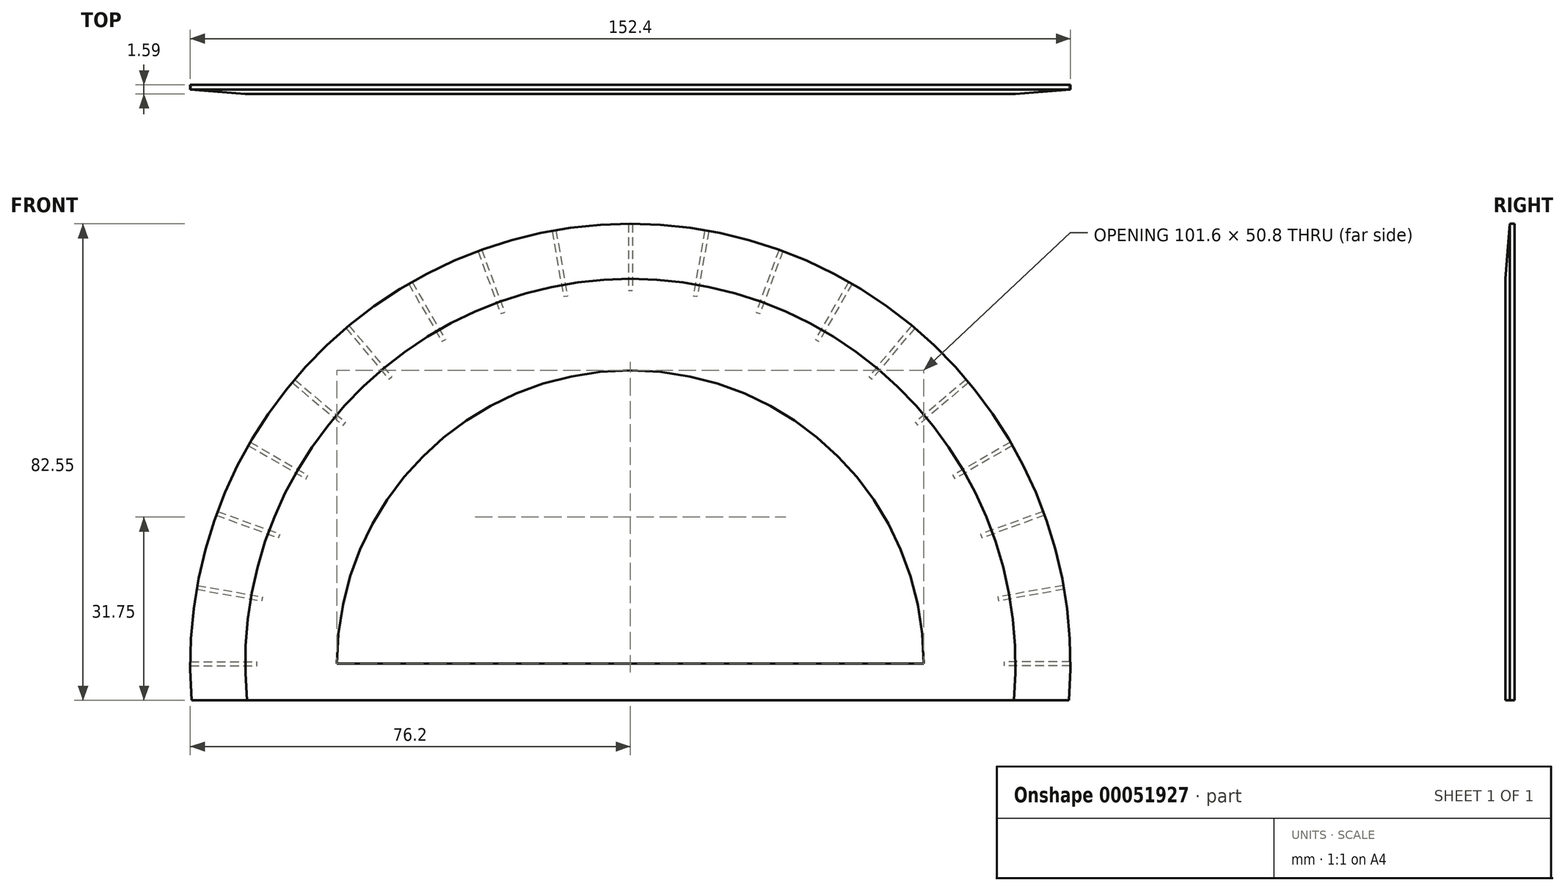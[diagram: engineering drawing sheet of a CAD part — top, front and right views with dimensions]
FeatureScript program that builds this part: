
annotation { "Feature Type Name" : "Feature", "Feature Type Description" : "" }
export const myFeature = defineFeature(function(context is Context, id is Id, definition is map)
    precondition{}
    {
        {
            var Q0;
            Q0=qCreatedBy(makeId("Front.planeOp"),FACE);
            var sketch = newSketch(context, id + "F0", { "sketchPlane" : qUnion([Q0])});
            skCircle(sketch, "E0", {"center": v(0, 0) * mm, "radius": 76.2 * mm});
            skCircle(sketch, "E1", {"center": v(0, 0) * mm, "radius": 50.8 * mm});
            skLineSegment(sketch, "E2", {"start": v(-50.8, 0) * mm, "end": v(50.8, 0) * mm});
            skLineSegment(sketch, "E3", {"start": v(-44, -25.4) * mm, "end": v(44, -25.4) * mm});
            skSolve(sketch);
        }
        {
            var Q0;
            Q0=makeQuery(id+"F0.imprint","IMPRINT",FACE,{"disambiguationData":[TD([[makeQuery(id+"F0.imprint","IMPRINT",EDGE,{"derivedFrom":sQuery(id+"F0.wireOp",EDGE,"E0")}),1.0]])]});
            var Q1;
            {var subQ0=sQuery(id+"F0.wireOp",EDGE,"E2");Q1=makeQuery(id+"F0.imprint","IMPRINT",FACE,{"disambiguationData":[TD([[makeQuery(id+"F0.imprint","IMPRINT",EDGE,{"derivedFrom":subQ0}),-1.0]])]});}
            extrude(context, id + "F1", {"entities" : qUnion([Q0, Q1]), "depth" : 1.59 * mm});
        }
        {
            var Q0;
            Q0=qCreatedBy(makeId("Top.planeOp"),FACE);
            var sketch = newSketch(context, id + "F2", { "sketchPlane" : qUnion([Q0])});
            skLineSegment(sketch, "E4", {"start": v(76.2, 0) * mm, "end": v(76.2, -1.59) * mm, "construction": true});
            skLineSegment(sketch, "E5.0", {"start": v(76.2, -1.59) * mm, "end": v(-76.2, -1.59) * mm, "construction": true});
            skLineSegment(sketch, "E6", {"start": v(76.2, -0.8) * mm, "end": v(66.67, -1.59) * mm});
            skLineSegment(sketch, "E7", {"start": v(66.67, -1.59) * mm, "end": v(76.2, -1.59) * mm});
            skLineSegment(sketch, "E8", {"start": v(0, 17.15) * mm, "end": v(0, -24.9) * mm, "construction": true});
            skLineSegment(sketch, "E9", {"start": v(76.2, -0.8) * mm, "end": v(76.2, -1.59) * mm});
            skSolve(sketch);
        }
        {
            var Q0;
            Q0=makeQuery(id+"F2.imprint","IMPRINT",FACE,{"disambiguationData":[TD([[makeQuery(id+"F2.imprint","IMPRINT",EDGE,{"derivedFrom":sQuery(id+"F2.wireOp",EDGE,"E6")}),1.0]])]});
            var Q1;
            Q1=sQuery(id+"F2.wireOp",EDGE,"E9");
            var Q2;
            Q2=sQuery(id+"F2.wireOp",EDGE,"E6");
            var Q3;
            Q3=sQuery(id+"F2.wireOp",EDGE,"E7");
            var Q4;
            Q4=sQuery(id+"F2.wireOp",EDGE,"E8");
            revolve(context, id + "F3", {"operationType" : NewBodyOperationType.REMOVE, "entities" : qUnion([Q0]), "surfaceEntities" : qUnion([Q1, Q2, Q3]), "axis" : qUnion([Q4]), "revolveType" : RevolveType.FULL, "oppositeDirection" : true});
        }
        {
            var Q0;
            Q0=makeQuery(id+"F1.opExtrude","CAP_FACE",FACE,{"disambiguationData":[OSD([sQuery(id+"F0.wireOp",EDGE,"E0"),sQuery(id+"F0.wireOp",EDGE,"E1"),sQuery(id+"F0.wireOp",EDGE,"E2"),sQuery(id+"F0.wireOp",EDGE,"E3")])],"isStart":true});
            var sketch = newSketch(context, id + "F4", { "sketchPlane" : qUnion([Q0])});
            skLineSegment(sketch, "E10.rect.bottom", {"start": v(76.2, -0.35) * mm, "end": v(64.66, -0.35) * mm});
            skLineSegment(sketch, "E10.rect.top", {"start": v(76.2, 0.35) * mm, "end": v(64.66, 0.35) * mm});
            skLineSegment(sketch, "E10.rect.left", {"start": v(76.2, -0.35) * mm, "end": v(76.2, 0.35) * mm});
            skLineSegment(sketch, "E10.rect.right", {"start": v(64.66, -0.35) * mm, "end": v(64.66, 0.35) * mm});
            skPoint(sketch, "E10.rect.middle", {"position": v(70.43, 0) * mm});
            skLineSegment(sketch, "E11.1.0", {"start": v(75.1, 12.9) * mm, "end": v(63.74, 10.89) * mm});
            skLineSegment(sketch, "E11.1.1", {"start": v(74.98, 13.57) * mm, "end": v(63.62, 11.57) * mm});
            skPoint(sketch, "E11.1.2", {"position": v(69.36, 12.23) * mm});
            skLineSegment(sketch, "E11.1.3", {"start": v(75.1, 12.9) * mm, "end": v(74.98, 13.57) * mm});
            skLineSegment(sketch, "E11.1.4", {"start": v(63.74, 10.89) * mm, "end": v(63.62, 11.57) * mm});
            skLineSegment(sketch, "E11.2.0", {"start": v(71.72, 25.74) * mm, "end": v(60.88, 21.8) * mm});
            skLineSegment(sketch, "E11.2.1", {"start": v(71.49, 26.39) * mm, "end": v(60.65, 22.44) * mm});
            skPoint(sketch, "E11.2.2", {"position": v(66.18, 24.09) * mm});
            skLineSegment(sketch, "E11.2.3", {"start": v(71.72, 25.74) * mm, "end": v(71.49, 26.39) * mm});
            skLineSegment(sketch, "E11.2.4", {"start": v(60.88, 21.8) * mm, "end": v(60.65, 22.44) * mm});
            skLineSegment(sketch, "E11.3.0", {"start": v(66.16, 37.8) * mm, "end": v(56.17, 32.03) * mm});
            skLineSegment(sketch, "E11.3.1", {"start": v(65.82, 38.4) * mm, "end": v(55.83, 32.63) * mm});
            skPoint(sketch, "E11.3.2", {"position": v(61, 35.22) * mm});
            skLineSegment(sketch, "E11.3.3", {"start": v(66.16, 37.8) * mm, "end": v(65.82, 38.4) * mm});
            skLineSegment(sketch, "E11.3.4", {"start": v(56.17, 32.03) * mm, "end": v(55.83, 32.63) * mm});
            skLineSegment(sketch, "E11.4.0", {"start": v(58.6, 48.71) * mm, "end": v(49.76, 41.3) * mm});
            skLineSegment(sketch, "E11.4.1", {"start": v(58.15, 49.25) * mm, "end": v(49.31, 41.83) * mm});
            skPoint(sketch, "E11.4.2", {"position": v(53.95, 45.27) * mm});
            skLineSegment(sketch, "E11.4.3", {"start": v(58.6, 48.71) * mm, "end": v(58.15, 49.25) * mm});
            skLineSegment(sketch, "E11.4.4", {"start": v(49.76, 41.3) * mm, "end": v(49.31, 41.83) * mm});
            skLineSegment(sketch, "E11.5.0", {"start": v(49.25, 58.15) * mm, "end": v(41.83, 49.31) * mm});
            skLineSegment(sketch, "E11.5.1", {"start": v(48.71, 58.6) * mm, "end": v(41.3, 49.76) * mm});
            skPoint(sketch, "E11.5.2", {"position": v(45.27, 53.95) * mm});
            skLineSegment(sketch, "E11.5.3", {"start": v(49.25, 58.15) * mm, "end": v(48.71, 58.6) * mm});
            skLineSegment(sketch, "E11.5.4", {"start": v(41.83, 49.31) * mm, "end": v(41.3, 49.76) * mm});
            skLineSegment(sketch, "E11.6.0", {"start": v(38.4, 65.82) * mm, "end": v(32.63, 55.83) * mm});
            skLineSegment(sketch, "E11.6.1", {"start": v(37.8, 66.16) * mm, "end": v(32.03, 56.17) * mm});
            skPoint(sketch, "E11.6.2", {"position": v(35.22, 61) * mm});
            skLineSegment(sketch, "E11.6.3", {"start": v(38.4, 65.82) * mm, "end": v(37.8, 66.16) * mm});
            skLineSegment(sketch, "E11.6.4", {"start": v(32.63, 55.83) * mm, "end": v(32.03, 56.17) * mm});
            skLineSegment(sketch, "E11.7.0", {"start": v(26.39, 71.49) * mm, "end": v(22.44, 60.65) * mm});
            skLineSegment(sketch, "E11.7.1", {"start": v(25.74, 71.72) * mm, "end": v(21.8, 60.88) * mm});
            skPoint(sketch, "E11.7.2", {"position": v(24.09, 66.18) * mm});
            skLineSegment(sketch, "E11.7.3", {"start": v(26.39, 71.49) * mm, "end": v(25.74, 71.72) * mm});
            skLineSegment(sketch, "E11.7.4", {"start": v(22.44, 60.65) * mm, "end": v(21.8, 60.88) * mm});
            skLineSegment(sketch, "E11.8.0", {"start": v(13.57, 74.98) * mm, "end": v(11.57, 63.62) * mm});
            skLineSegment(sketch, "E11.8.1", {"start": v(12.9, 75.1) * mm, "end": v(10.89, 63.74) * mm});
            skPoint(sketch, "E11.8.2", {"position": v(12.23, 69.36) * mm});
            skLineSegment(sketch, "E11.8.3", {"start": v(13.57, 74.98) * mm, "end": v(12.9, 75.1) * mm});
            skLineSegment(sketch, "E11.8.4", {"start": v(11.57, 63.62) * mm, "end": v(10.89, 63.74) * mm});
            skLineSegment(sketch, "E11.9.0", {"start": v(0.35, 76.2) * mm, "end": v(0.35, 64.66) * mm});
            skLineSegment(sketch, "E11.9.1", {"start": v(-0.35, 76.2) * mm, "end": v(-0.35, 64.66) * mm});
            skPoint(sketch, "E11.9.2", {"position": v(0, 70.43) * mm});
            skLineSegment(sketch, "E11.9.3", {"start": v(0.35, 76.2) * mm, "end": v(-0.35, 76.2) * mm});
            skLineSegment(sketch, "E11.9.4", {"start": v(0.35, 64.66) * mm, "end": v(-0.35, 64.66) * mm});
            skLineSegment(sketch, "E11.10.0", {"start": v(-12.9, 75.1) * mm, "end": v(-10.89, 63.74) * mm});
            skLineSegment(sketch, "E11.10.1", {"start": v(-13.57, 74.98) * mm, "end": v(-11.57, 63.62) * mm});
            skPoint(sketch, "E11.10.2", {"position": v(-12.23, 69.36) * mm});
            skLineSegment(sketch, "E11.10.3", {"start": v(-12.9, 75.1) * mm, "end": v(-13.57, 74.98) * mm});
            skLineSegment(sketch, "E11.10.4", {"start": v(-10.89, 63.74) * mm, "end": v(-11.57, 63.62) * mm});
            skLineSegment(sketch, "E11.11.0", {"start": v(-25.74, 71.72) * mm, "end": v(-21.8, 60.88) * mm});
            skLineSegment(sketch, "E11.11.1", {"start": v(-26.39, 71.49) * mm, "end": v(-22.44, 60.65) * mm});
            skPoint(sketch, "E11.11.2", {"position": v(-24.09, 66.18) * mm});
            skLineSegment(sketch, "E11.11.3", {"start": v(-25.74, 71.72) * mm, "end": v(-26.39, 71.49) * mm});
            skLineSegment(sketch, "E11.11.4", {"start": v(-21.8, 60.88) * mm, "end": v(-22.44, 60.65) * mm});
            skLineSegment(sketch, "E11.12.0", {"start": v(-37.8, 66.16) * mm, "end": v(-32.03, 56.17) * mm});
            skLineSegment(sketch, "E11.12.1", {"start": v(-38.4, 65.82) * mm, "end": v(-32.63, 55.83) * mm});
            skPoint(sketch, "E11.12.2", {"position": v(-35.22, 61) * mm});
            skLineSegment(sketch, "E11.12.3", {"start": v(-37.8, 66.16) * mm, "end": v(-38.4, 65.82) * mm});
            skLineSegment(sketch, "E11.12.4", {"start": v(-32.03, 56.17) * mm, "end": v(-32.63, 55.83) * mm});
            skLineSegment(sketch, "E11.13.0", {"start": v(-48.71, 58.6) * mm, "end": v(-41.3, 49.76) * mm});
            skLineSegment(sketch, "E11.13.1", {"start": v(-49.25, 58.15) * mm, "end": v(-41.83, 49.31) * mm});
            skPoint(sketch, "E11.13.2", {"position": v(-45.27, 53.95) * mm});
            skLineSegment(sketch, "E11.13.3", {"start": v(-48.71, 58.6) * mm, "end": v(-49.25, 58.15) * mm});
            skLineSegment(sketch, "E11.13.4", {"start": v(-41.3, 49.76) * mm, "end": v(-41.83, 49.31) * mm});
            skLineSegment(sketch, "E11.14.0", {"start": v(-58.15, 49.25) * mm, "end": v(-49.31, 41.83) * mm});
            skLineSegment(sketch, "E11.14.1", {"start": v(-58.6, 48.71) * mm, "end": v(-49.76, 41.3) * mm});
            skPoint(sketch, "E11.14.2", {"position": v(-53.95, 45.27) * mm});
            skLineSegment(sketch, "E11.14.3", {"start": v(-58.15, 49.25) * mm, "end": v(-58.6, 48.71) * mm});
            skLineSegment(sketch, "E11.14.4", {"start": v(-49.31, 41.83) * mm, "end": v(-49.76, 41.3) * mm});
            skLineSegment(sketch, "E11.15.0", {"start": v(-65.82, 38.4) * mm, "end": v(-55.83, 32.63) * mm});
            skLineSegment(sketch, "E11.15.1", {"start": v(-66.16, 37.8) * mm, "end": v(-56.17, 32.03) * mm});
            skPoint(sketch, "E11.15.2", {"position": v(-61, 35.22) * mm});
            skLineSegment(sketch, "E11.15.3", {"start": v(-65.82, 38.4) * mm, "end": v(-66.16, 37.8) * mm});
            skLineSegment(sketch, "E11.15.4", {"start": v(-55.83, 32.63) * mm, "end": v(-56.17, 32.03) * mm});
            skLineSegment(sketch, "E11.16.0", {"start": v(-71.49, 26.39) * mm, "end": v(-60.65, 22.44) * mm});
            skLineSegment(sketch, "E11.16.1", {"start": v(-71.72, 25.74) * mm, "end": v(-60.88, 21.8) * mm});
            skPoint(sketch, "E11.16.2", {"position": v(-66.18, 24.09) * mm});
            skLineSegment(sketch, "E11.16.3", {"start": v(-71.49, 26.39) * mm, "end": v(-71.72, 25.74) * mm});
            skLineSegment(sketch, "E11.16.4", {"start": v(-60.65, 22.44) * mm, "end": v(-60.88, 21.8) * mm});
            skLineSegment(sketch, "E11.17.0", {"start": v(-74.98, 13.57) * mm, "end": v(-63.62, 11.57) * mm});
            skLineSegment(sketch, "E11.17.1", {"start": v(-75.1, 12.9) * mm, "end": v(-63.74, 10.89) * mm});
            skPoint(sketch, "E11.17.2", {"position": v(-69.36, 12.23) * mm});
            skLineSegment(sketch, "E11.17.3", {"start": v(-74.98, 13.57) * mm, "end": v(-75.1, 12.9) * mm});
            skLineSegment(sketch, "E11.17.4", {"start": v(-63.62, 11.57) * mm, "end": v(-63.74, 10.89) * mm});
            skLineSegment(sketch, "E11.18.0", {"start": v(-76.2, 0.35) * mm, "end": v(-64.66, 0.35) * mm});
            skLineSegment(sketch, "E11.18.1", {"start": v(-76.2, -0.35) * mm, "end": v(-64.66, -0.35) * mm});
            skPoint(sketch, "E11.18.2", {"position": v(-70.43, 0) * mm});
            skLineSegment(sketch, "E11.18.3", {"start": v(-76.2, 0.35) * mm, "end": v(-76.2, -0.35) * mm});
            skLineSegment(sketch, "E11.18.4", {"start": v(-64.66, 0.35) * mm, "end": v(-64.66, -0.35) * mm});
            skLineSegment(sketch, "E11.19.0", {"start": v(-75.1, -12.9) * mm, "end": v(-63.74, -10.89) * mm});
            skLineSegment(sketch, "E11.19.1", {"start": v(-74.98, -13.57) * mm, "end": v(-63.62, -11.57) * mm});
            skPoint(sketch, "E11.19.2", {"position": v(-69.36, -12.23) * mm});
            skLineSegment(sketch, "E11.19.3", {"start": v(-75.1, -12.9) * mm, "end": v(-74.98, -13.57) * mm});
            skLineSegment(sketch, "E11.19.4", {"start": v(-63.74, -10.89) * mm, "end": v(-63.62, -11.57) * mm});
            skLineSegment(sketch, "E11.20.0", {"start": v(-71.72, -25.74) * mm, "end": v(-60.88, -21.8) * mm});
            skLineSegment(sketch, "E11.20.1", {"start": v(-71.49, -26.39) * mm, "end": v(-60.65, -22.44) * mm});
            skPoint(sketch, "E11.20.2", {"position": v(-66.18, -24.09) * mm});
            skLineSegment(sketch, "E11.20.3", {"start": v(-71.72, -25.74) * mm, "end": v(-71.49, -26.39) * mm});
            skLineSegment(sketch, "E11.20.4", {"start": v(-60.88, -21.8) * mm, "end": v(-60.65, -22.44) * mm});
            skLineSegment(sketch, "E11.21.0", {"start": v(-66.16, -37.8) * mm, "end": v(-56.17, -32.03) * mm});
            skLineSegment(sketch, "E11.21.1", {"start": v(-65.82, -38.4) * mm, "end": v(-55.83, -32.63) * mm});
            skPoint(sketch, "E11.21.2", {"position": v(-61, -35.22) * mm});
            skLineSegment(sketch, "E11.21.3", {"start": v(-66.16, -37.8) * mm, "end": v(-65.82, -38.4) * mm});
            skLineSegment(sketch, "E11.21.4", {"start": v(-56.17, -32.03) * mm, "end": v(-55.83, -32.63) * mm});
            skLineSegment(sketch, "E11.22.0", {"start": v(-58.6, -48.71) * mm, "end": v(-49.76, -41.3) * mm});
            skLineSegment(sketch, "E11.22.1", {"start": v(-58.15, -49.25) * mm, "end": v(-49.31, -41.83) * mm});
            skPoint(sketch, "E11.22.2", {"position": v(-53.95, -45.27) * mm});
            skLineSegment(sketch, "E11.22.3", {"start": v(-58.6, -48.71) * mm, "end": v(-58.15, -49.25) * mm});
            skLineSegment(sketch, "E11.22.4", {"start": v(-49.76, -41.3) * mm, "end": v(-49.31, -41.83) * mm});
            skLineSegment(sketch, "E11.23.0", {"start": v(-49.25, -58.15) * mm, "end": v(-41.83, -49.31) * mm});
            skLineSegment(sketch, "E11.23.1", {"start": v(-48.71, -58.6) * mm, "end": v(-41.3, -49.76) * mm});
            skPoint(sketch, "E11.23.2", {"position": v(-45.27, -53.95) * mm});
            skLineSegment(sketch, "E11.23.3", {"start": v(-49.25, -58.15) * mm, "end": v(-48.71, -58.6) * mm});
            skLineSegment(sketch, "E11.23.4", {"start": v(-41.83, -49.31) * mm, "end": v(-41.3, -49.76) * mm});
            skLineSegment(sketch, "E11.24.0", {"start": v(-38.4, -65.82) * mm, "end": v(-32.63, -55.83) * mm});
            skLineSegment(sketch, "E11.24.1", {"start": v(-37.8, -66.16) * mm, "end": v(-32.03, -56.17) * mm});
            skPoint(sketch, "E11.24.2", {"position": v(-35.22, -61) * mm});
            skLineSegment(sketch, "E11.24.3", {"start": v(-38.4, -65.82) * mm, "end": v(-37.8, -66.16) * mm});
            skLineSegment(sketch, "E11.24.4", {"start": v(-32.63, -55.83) * mm, "end": v(-32.03, -56.17) * mm});
            skLineSegment(sketch, "E11.25.0", {"start": v(-26.39, -71.49) * mm, "end": v(-22.44, -60.65) * mm});
            skLineSegment(sketch, "E11.25.1", {"start": v(-25.74, -71.72) * mm, "end": v(-21.8, -60.88) * mm});
            skPoint(sketch, "E11.25.2", {"position": v(-24.09, -66.18) * mm});
            skLineSegment(sketch, "E11.25.3", {"start": v(-26.39, -71.49) * mm, "end": v(-25.74, -71.72) * mm});
            skLineSegment(sketch, "E11.25.4", {"start": v(-22.44, -60.65) * mm, "end": v(-21.8, -60.88) * mm});
            skLineSegment(sketch, "E11.26.0", {"start": v(-13.57, -74.98) * mm, "end": v(-11.57, -63.62) * mm});
            skLineSegment(sketch, "E11.26.1", {"start": v(-12.9, -75.1) * mm, "end": v(-10.89, -63.74) * mm});
            skPoint(sketch, "E11.26.2", {"position": v(-12.23, -69.36) * mm});
            skLineSegment(sketch, "E11.26.3", {"start": v(-13.57, -74.98) * mm, "end": v(-12.9, -75.1) * mm});
            skLineSegment(sketch, "E11.26.4", {"start": v(-11.57, -63.62) * mm, "end": v(-10.89, -63.74) * mm});
            skLineSegment(sketch, "E11.27.0", {"start": v(-0.35, -76.2) * mm, "end": v(-0.35, -64.66) * mm});
            skLineSegment(sketch, "E11.27.1", {"start": v(0.35, -76.2) * mm, "end": v(0.35, -64.66) * mm});
            skPoint(sketch, "E11.27.2", {"position": v(0, -70.43) * mm});
            skLineSegment(sketch, "E11.27.3", {"start": v(-0.35, -76.2) * mm, "end": v(0.35, -76.2) * mm});
            skLineSegment(sketch, "E11.27.4", {"start": v(-0.35, -64.66) * mm, "end": v(0.35, -64.66) * mm});
            skLineSegment(sketch, "E11.28.0", {"start": v(12.9, -75.1) * mm, "end": v(10.89, -63.74) * mm});
            skLineSegment(sketch, "E11.28.1", {"start": v(13.57, -74.98) * mm, "end": v(11.57, -63.62) * mm});
            skPoint(sketch, "E11.28.2", {"position": v(12.23, -69.36) * mm});
            skLineSegment(sketch, "E11.28.3", {"start": v(12.9, -75.1) * mm, "end": v(13.57, -74.98) * mm});
            skLineSegment(sketch, "E11.28.4", {"start": v(10.89, -63.74) * mm, "end": v(11.57, -63.62) * mm});
            skLineSegment(sketch, "E11.29.0", {"start": v(25.74, -71.72) * mm, "end": v(21.8, -60.88) * mm});
            skLineSegment(sketch, "E11.29.1", {"start": v(26.39, -71.49) * mm, "end": v(22.44, -60.65) * mm});
            skPoint(sketch, "E11.29.2", {"position": v(24.09, -66.18) * mm});
            skLineSegment(sketch, "E11.29.3", {"start": v(25.74, -71.72) * mm, "end": v(26.39, -71.49) * mm});
            skLineSegment(sketch, "E11.29.4", {"start": v(21.8, -60.88) * mm, "end": v(22.44, -60.65) * mm});
            skLineSegment(sketch, "E11.30.0", {"start": v(37.8, -66.16) * mm, "end": v(32.03, -56.17) * mm});
            skLineSegment(sketch, "E11.30.1", {"start": v(38.4, -65.82) * mm, "end": v(32.63, -55.83) * mm});
            skPoint(sketch, "E11.30.2", {"position": v(35.22, -61) * mm});
            skLineSegment(sketch, "E11.30.3", {"start": v(37.8, -66.16) * mm, "end": v(38.4, -65.82) * mm});
            skLineSegment(sketch, "E11.30.4", {"start": v(32.03, -56.17) * mm, "end": v(32.63, -55.83) * mm});
            skLineSegment(sketch, "E11.31.0", {"start": v(48.71, -58.6) * mm, "end": v(41.3, -49.76) * mm});
            skLineSegment(sketch, "E11.31.1", {"start": v(49.25, -58.15) * mm, "end": v(41.83, -49.31) * mm});
            skPoint(sketch, "E11.31.2", {"position": v(45.27, -53.95) * mm});
            skLineSegment(sketch, "E11.31.3", {"start": v(48.71, -58.6) * mm, "end": v(49.25, -58.15) * mm});
            skLineSegment(sketch, "E11.31.4", {"start": v(41.3, -49.76) * mm, "end": v(41.83, -49.31) * mm});
            skLineSegment(sketch, "E11.32.0", {"start": v(58.15, -49.25) * mm, "end": v(49.31, -41.83) * mm});
            skLineSegment(sketch, "E11.32.1", {"start": v(58.6, -48.71) * mm, "end": v(49.76, -41.3) * mm});
            skPoint(sketch, "E11.32.2", {"position": v(53.95, -45.27) * mm});
            skLineSegment(sketch, "E11.32.3", {"start": v(58.15, -49.25) * mm, "end": v(58.6, -48.71) * mm});
            skLineSegment(sketch, "E11.32.4", {"start": v(49.31, -41.83) * mm, "end": v(49.76, -41.3) * mm});
            skLineSegment(sketch, "E11.33.0", {"start": v(65.82, -38.4) * mm, "end": v(55.83, -32.63) * mm});
            skLineSegment(sketch, "E11.33.1", {"start": v(66.16, -37.8) * mm, "end": v(56.17, -32.03) * mm});
            skPoint(sketch, "E11.33.2", {"position": v(61, -35.22) * mm});
            skLineSegment(sketch, "E11.33.3", {"start": v(65.82, -38.4) * mm, "end": v(66.16, -37.8) * mm});
            skLineSegment(sketch, "E11.33.4", {"start": v(55.83, -32.63) * mm, "end": v(56.17, -32.03) * mm});
            skLineSegment(sketch, "E11.34.0", {"start": v(71.49, -26.39) * mm, "end": v(60.65, -22.44) * mm});
            skLineSegment(sketch, "E11.34.1", {"start": v(71.72, -25.74) * mm, "end": v(60.88, -21.8) * mm});
            skPoint(sketch, "E11.34.2", {"position": v(66.18, -24.09) * mm});
            skLineSegment(sketch, "E11.34.3", {"start": v(71.49, -26.39) * mm, "end": v(71.72, -25.74) * mm});
            skLineSegment(sketch, "E11.34.4", {"start": v(60.65, -22.44) * mm, "end": v(60.88, -21.8) * mm});
            skLineSegment(sketch, "E11.35.0", {"start": v(74.98, -13.57) * mm, "end": v(63.62, -11.57) * mm});
            skLineSegment(sketch, "E11.35.1", {"start": v(75.1, -12.9) * mm, "end": v(63.74, -10.89) * mm});
            skPoint(sketch, "E11.35.2", {"position": v(69.36, -12.23) * mm});
            skLineSegment(sketch, "E11.35.3", {"start": v(74.98, -13.57) * mm, "end": v(75.1, -12.9) * mm});
            skLineSegment(sketch, "E11.35.4", {"start": v(63.62, -11.57) * mm, "end": v(63.74, -10.89) * mm});
            skPoint(sketch, "E11.center", {"position": v(0, 0) * mm});
            skSolve(sketch);
        }
        {
            var Q0;
            Q0=qSketchRegion(id+"F4",true);
            extrude(context, id + "F5", {"entities" : qUnion([Q0]), "operationType" : NewBodyOperationType.REMOVE, "oppositeDirection" : true, "depth" : 0.03 * mm});
        }
        {
            var Q0;
            Q0=qCreatedBy(makeId("Front.planeOp"),FACE);
            var sketch = newSketch(context, id + "F6", { "sketchPlane" : qUnion([Q0])});
            skLineSegment(sketch, "E12.rect.bottom", {"start": v(87.6, -82.88) * mm, "end": v(-87.6, -82.88) * mm});
            skLineSegment(sketch, "E12.rect.top", {"start": v(87.6, -6.35) * mm, "end": v(-87.6, -6.35) * mm});
            skLineSegment(sketch, "E12.rect.left", {"start": v(87.6, -82.88) * mm, "end": v(87.6, -6.35) * mm});
            skLineSegment(sketch, "E12.rect.right", {"start": v(-87.6, -82.88) * mm, "end": v(-87.6, -6.35) * mm});
            skPoint(sketch, "E12.rect.middle", {"position": v(0, -44.61) * mm});
            skSolve(sketch);
        }
        {
            var Q0;
            Q0=makeQuery(id+"F6.imprint","IMPRINT",FACE,{"disambiguationData":[TD([[makeQuery(id+"F6.imprint","IMPRINT",EDGE,{"derivedFrom":sQuery(id+"F6.wireOp",EDGE,"E12.rect.bottom")}),-1.0]])]});
            extrude(context, id + "F7", {"entities" : qUnion([Q0]), "operationType" : NewBodyOperationType.REMOVE, "depth" : 25.4 * mm});
        }
    });
